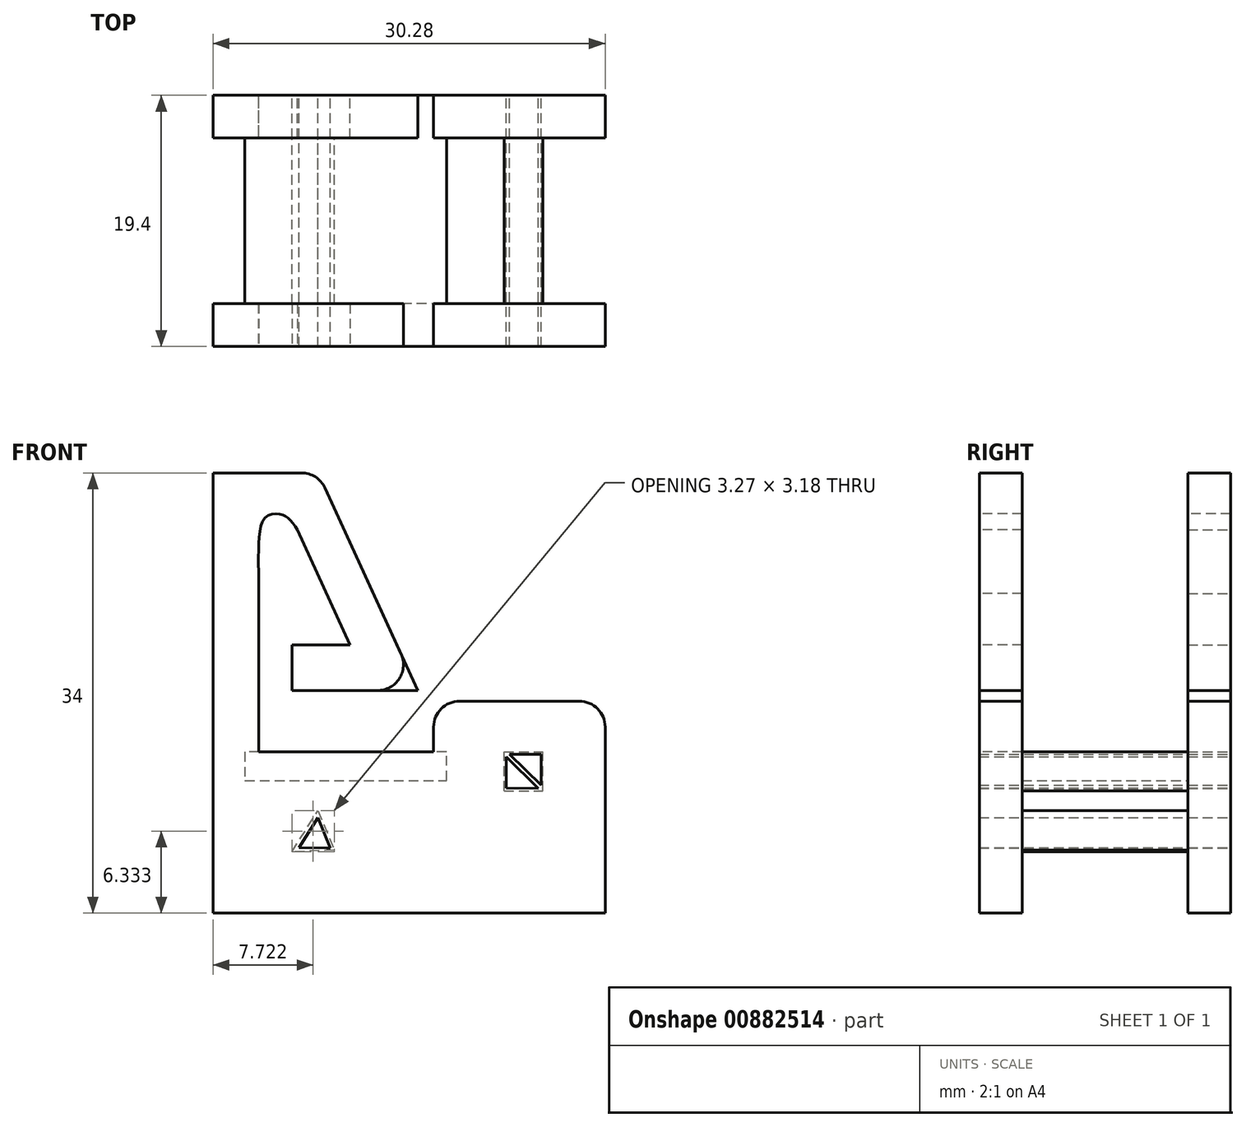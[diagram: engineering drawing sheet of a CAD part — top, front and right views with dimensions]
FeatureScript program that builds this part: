
annotation { "Feature Type Name" : "Feature", "Feature Type Description" : "" }
export const myFeature = defineFeature(function(context is Context, id is Id, definition is map)
    precondition{}
    {
        {
            var Q0;
            Q0=qCreatedBy(makeId("Front.planeOp"),FACE);
            var sketch = newSketch(context, id + "F0", { "sketchPlane" : qUnion([Q0])});
            skLineSegment(sketch, "E0", {"start": v(0, 0) * mm, "end": v(0, 34) * mm});
            skLineSegment(sketch, "E1", {"start": v(0, 34) * mm, "end": v(8.1, 34) * mm});
            skLineSegment(sketch, "E2", {"start": v(8.1, 34) * mm, "end": v(15.82, 17.2) * mm});
            skLineSegment(sketch, "E3", {"start": v(15.82, 17.2) * mm, "end": v(6.11, 17.2) * mm});
            skLineSegment(sketch, "E4", {"start": v(6.11, 17.2) * mm, "end": v(6.11, 20.72) * mm});
            skLineSegment(sketch, "E5", {"start": v(6.11, 20.72) * mm, "end": v(10.6, 20.72) * mm});
            skLineSegment(sketch, "E6", {"start": v(10.6, 20.72) * mm, "end": v(6.52, 29.6) * mm});
            skFitSpline(sketch, "E7", {"points": [v(6.52, 29.6) * mm, v(5.83, 30.48) * mm, v(5.16, 30.81) * mm, v(4.07, 30.57) * mm, v(3.54, 28.62) * mm, v(3.54, 24.67) * mm], "startDerivative": vector(-4.1, 6.02) * mm, "endDerivative": vector(0.29, -13.32) * mm});
            skLineSegment(sketch, "E8", {"start": v(3.54, 24.67) * mm, "end": v(3.54, 12.45) * mm});
            skLineSegment(sketch, "E9", {"start": v(3.54, 12.45) * mm, "end": v(2.46, 12.45) * mm});
            skLineSegment(sketch, "E10", {"start": v(2.46, 12.45) * mm, "end": v(2.46, 10.25) * mm});
            skLineSegment(sketch, "E11", {"start": v(2.46, 10.25) * mm, "end": v(18.04, 10.25) * mm});
            skLineSegment(sketch, "E12", {"start": v(18.04, 10.25) * mm, "end": v(18.04, 12.45) * mm});
            skLineSegment(sketch, "E13", {"start": v(18.04, 12.45) * mm, "end": v(17.04, 12.45) * mm});
            skLineSegment(sketch, "E14", {"start": v(17.04, 12.45) * mm, "end": v(17.04, 16.37) * mm});
            skLineSegment(sketch, "E15", {"start": v(17.04, 16.37) * mm, "end": v(30.28, 16.37) * mm});
            skLineSegment(sketch, "E16", {"start": v(30.28, 16.37) * mm, "end": v(30.28, 0) * mm});
            skLineSegment(sketch, "E17", {"start": v(30.28, 0) * mm, "end": v(0, 0) * mm});
            skLineSegment(sketch, "E18", {"start": v(22.47, 9.45) * mm, "end": v(22.47, 12.45) * mm});
            skLineSegment(sketch, "E19", {"start": v(22.47, 12.45) * mm, "end": v(25.47, 12.45) * mm});
            skLineSegment(sketch, "E20", {"start": v(22.47, 9.45) * mm, "end": v(25.47, 9.45) * mm});
            skLineSegment(sketch, "E21", {"start": v(25.47, 9.45) * mm, "end": v(25.47, 12.45) * mm});
            skSolve(sketch);
        }
        {
            var Q0;
            Q0 = qSketchRegion(id + "F0", true);
            extrude(context, id + "F1", {"entities" : qUnion([Q0]), "depth" : 3.3 * mm, "offsetDistance" : 25 * mm});
        }
        {
            var Q0;
            Q0=makeQuery(id+"F1.opExtrude","CAP_FACE",FACE,{"disambiguationData":[OSD([sQuery(id+"F0.wireOp",EDGE,"E0"),sQuery(id+"F0.wireOp",EDGE,"E1"),sQuery(id+"F0.wireOp",EDGE,"E2"),sQuery(id+"F0.wireOp",EDGE,"E3"),sQuery(id+"F0.wireOp",EDGE,"E4"),sQuery(id+"F0.wireOp",EDGE,"E5"),sQuery(id+"F0.wireOp",EDGE,"E6"),sQuery(id+"F0.wireOp",EDGE,"E7"),sQuery(id+"F0.wireOp",EDGE,"E8"),sQuery(id+"F0.wireOp",EDGE,"E9"),sQuery(id+"F0.wireOp",EDGE,"E10"),sQuery(id+"F0.wireOp",EDGE,"E11"),sQuery(id+"F0.wireOp",EDGE,"E12"),sQuery(id+"F0.wireOp",EDGE,"E13"),sQuery(id+"F0.wireOp",EDGE,"E14"),sQuery(id+"F0.wireOp",EDGE,"E15"),sQuery(id+"F0.wireOp",EDGE,"E16"),sQuery(id+"F0.wireOp",EDGE,"E17"),sQuery(id+"F0.wireOp",EDGE,"E18"),sQuery(id+"F0.wireOp",EDGE,"E19"),sQuery(id+"F0.wireOp",EDGE,"E20"),sQuery(id+"F0.wireOp",EDGE,"E21")])],"isStart":true});
            var sketch = newSketch(context, id + "F2", { "sketchPlane" : qUnion([Q0])});
            skLineSegment(sketch, "E22", {"start": v(-9.36, 4.88) * mm, "end": v(-8.1, 7.92) * mm});
            skLineSegment(sketch, "E23", {"start": v(-8.1, 7.92) * mm, "end": v(-6.09, 4.74) * mm});
            skLineSegment(sketch, "E24", {"start": v(-6.09, 4.74) * mm, "end": v(-9.36, 4.88) * mm});
            skLineSegment(sketch, "E25", {"start": v(-25.47, 9.45) * mm, "end": v(-22.47, 12.45) * mm});
            skLineSegment(sketch, "E26", {"start": v(-22.47, 12.45) * mm, "end": v(-25.47, 12.45) * mm});
            skLineSegment(sketch, "E27", {"start": v(-25.47, 12.45) * mm, "end": v(-25.47, 9.45) * mm});
            skLineSegment(sketch, "E28", {"start": v(-25.47, 9.45) * mm, "end": v(-22.47, 9.45) * mm});
            skLineSegment(sketch, "E29", {"start": v(-22.47, 9.45) * mm, "end": v(-22.47, 12.45) * mm});
            skLineSegment(sketch, "E30", {"start": v(-25.11, 9.63) * mm, "end": v(-22.65, 12.09) * mm});
            skLineSegment(sketch, "E31", {"start": v(-22.65, 12.09) * mm, "end": v(-22.65, 9.68) * mm});
            skLineSegment(sketch, "E32", {"start": v(-22.65, 9.68) * mm, "end": v(-25.11, 9.63) * mm});
            skLineSegment(sketch, "E33", {"start": v(-25.34, 9.89) * mm, "end": v(-25.34, 12.27) * mm});
            skLineSegment(sketch, "E34", {"start": v(-25.34, 12.27) * mm, "end": v(-22.9, 12.27) * mm});
            skLineSegment(sketch, "E35", {"start": v(-22.9, 12.27) * mm, "end": v(-25.34, 9.89) * mm});
            skLineSegment(sketch, "E36", {"start": v(-8.78, 5.03) * mm, "end": v(-9.04, 5.03) * mm});
            skLineSegment(sketch, "E37", {"start": v(-9.04, 5.03) * mm, "end": v(-8.1, 7.37) * mm});
            skLineSegment(sketch, "E38", {"start": v(-8.1, 7.37) * mm, "end": v(-6.62, 5.05) * mm});
            skLineSegment(sketch, "E39", {"start": v(-6.62, 5.05) * mm, "end": v(-8.78, 5.03) * mm});
            skSolve(sketch);
        }
        {
            var Q0;
            Q0 = qSketchRegion(id + "F2", true);
            extrude(context, id + "F3", {"entities" : qUnion([Q0]), "operationType" : NewBodyOperationType.ADD, "oppositeDirection" : true, "depth" : 9.7 * mm, "offsetDistance" : 25 * mm});
        }
        {
            var Q0;
            Q0=makeQuery(id+"F2.imprint","IMPRINT",FACE,{"disambiguationData":[TD([[makeQuery(id+"F2.imprint","IMPRINT",EDGE,{"derivedFrom":sQuery(id+"F2.wireOp",EDGE,"E36")}),-1.0]])]});
            extrude(context, id + "F4", {"entities" : qUnion([Q0]), "operationType" : NewBodyOperationType.REMOVE, "oppositeDirection" : true, "depth" : 25 * mm, "offsetDistance" : 25 * mm});
        }
        {
            var Q0;
            Q0=makeQuery(id+"F3.boolean.opBoolean","MERGE",FACE,{"derivedFrom":[makeQuery(id+"F1.opExtrude","CAP_FACE",FACE,{"disambiguationData":[OSD([sQuery(id+"F0.wireOp",EDGE,"E0"),sQuery(id+"F0.wireOp",EDGE,"E1"),sQuery(id+"F0.wireOp",EDGE,"E2"),sQuery(id+"F0.wireOp",EDGE,"E3"),sQuery(id+"F0.wireOp",EDGE,"E4"),sQuery(id+"F0.wireOp",EDGE,"E5"),sQuery(id+"F0.wireOp",EDGE,"E6"),sQuery(id+"F0.wireOp",EDGE,"E7"),sQuery(id+"F0.wireOp",EDGE,"E8"),sQuery(id+"F0.wireOp",EDGE,"E9"),sQuery(id+"F0.wireOp",EDGE,"E10"),sQuery(id+"F0.wireOp",EDGE,"E11"),sQuery(id+"F0.wireOp",EDGE,"E12"),sQuery(id+"F0.wireOp",EDGE,"E13"),sQuery(id+"F0.wireOp",EDGE,"E14"),sQuery(id+"F0.wireOp",EDGE,"E15"),sQuery(id+"F0.wireOp",EDGE,"E16"),sQuery(id+"F0.wireOp",EDGE,"E17"),sQuery(id+"F0.wireOp",EDGE,"E18"),sQuery(id+"F0.wireOp",EDGE,"E19"),sQuery(id+"F0.wireOp",EDGE,"E20"),sQuery(id+"F0.wireOp",EDGE,"E21")])],"isStart":true}),makeQuery(id+"F3.opExtrude","CAP_FACE",FACE,{"disambiguationData":[OSD([sQuery(id+"F2.wireOp",EDGE,"E26"),sQuery(id+"F2.wireOp",EDGE,"E27"),sQuery(id+"F2.wireOp",EDGE,"E28"),sQuery(id+"F2.wireOp",EDGE,"E29"),sQuery(id+"F2.wireOp",EDGE,"E30"),sQuery(id+"F2.wireOp",EDGE,"E31"),sQuery(id+"F2.wireOp",EDGE,"E32"),sQuery(id+"F2.wireOp",EDGE,"E33"),sQuery(id+"F2.wireOp",EDGE,"E34"),sQuery(id+"F2.wireOp",EDGE,"E35")])],"isStart":true})]});
            var sketch = newSketch(context, id + "F5", { "sketchPlane" : qUnion([Q0])});
            skLineSegment(sketch, "E40", {"start": v(-18.04, 10.25) * mm, "end": v(-18.04, 12.45) * mm});
            skLineSegment(sketch, "E41", {"start": v(-18.04, 12.45) * mm, "end": v(-2.46, 12.45) * mm});
            skLineSegment(sketch, "E42", {"start": v(-2.46, 12.45) * mm, "end": v(-2.46, 10.25) * mm});
            skLineSegment(sketch, "E43", {"start": v(-2.46, 10.25) * mm, "end": v(-18.04, 10.25) * mm});
            skSolve(sketch);
        }
        {
            var Q0;
            Q0 = qSketchRegion(id + "F5", true);
            extrude(context, id + "F6", {"entities" : qUnion([Q0]), "operationType" : NewBodyOperationType.ADD, "oppositeDirection" : true, "depth" : 9.7 * mm, "offsetDistance" : 25 * mm});
        }
        {
            var Q0;
            Q0=makeQuery(id+"F1.opExtrude","SWEPT_BODY",BODY,{"disambiguationData":[OSD([sQuery(id+"F0.wireOp",EDGE,"E0"),sQuery(id+"F0.wireOp",EDGE,"E1"),sQuery(id+"F0.wireOp",EDGE,"E2"),sQuery(id+"F0.wireOp",EDGE,"E3"),sQuery(id+"F0.wireOp",EDGE,"E4"),sQuery(id+"F0.wireOp",EDGE,"E5"),sQuery(id+"F0.wireOp",EDGE,"E6"),sQuery(id+"F0.wireOp",EDGE,"E7"),sQuery(id+"F0.wireOp",EDGE,"E8"),sQuery(id+"F0.wireOp",EDGE,"E9"),sQuery(id+"F0.wireOp",EDGE,"E10"),sQuery(id+"F0.wireOp",EDGE,"E11"),sQuery(id+"F0.wireOp",EDGE,"E12"),sQuery(id+"F0.wireOp",EDGE,"E13"),sQuery(id+"F0.wireOp",EDGE,"E14"),sQuery(id+"F0.wireOp",EDGE,"E15"),sQuery(id+"F0.wireOp",EDGE,"E16"),sQuery(id+"F0.wireOp",EDGE,"E17"),sQuery(id+"F0.wireOp",EDGE,"E18"),sQuery(id+"F0.wireOp",EDGE,"E19"),sQuery(id+"F0.wireOp",EDGE,"E20"),sQuery(id+"F0.wireOp",EDGE,"E21")])]});
            var Q1;
            Q1=makeQuery(id+"F6.opExtrude","CAP_FACE",FACE,{"disambiguationData":[OSD([sQuery(id+"F5.wireOp",EDGE,"E40"),sQuery(id+"F5.wireOp",EDGE,"E41"),sQuery(id+"F5.wireOp",EDGE,"E42"),sQuery(id+"F5.wireOp",EDGE,"E43")])],"isStart":false});
            mirror(context, id + "F7", {"operationType" : NewBodyOperationType.ADD, "entities" : qUnion([Q0]), "mirrorPlane" : qUnion([Q1])});
        }
        {
            var Q0;
            Q0=makeQuery(id+"F7.opPattern","COPY",EDGE,{"derivedFrom":makeQuery(id+"F1.opExtrude","SWEPT_EDGE",EDGE,{"disambiguationData":[OSD([sQuery(id+"F0.wireOp",EDGE,"E15"),sQuery(id+"F0.wireOp",EDGE,"E16")])]}),"instanceName":"1"});
            var Q1;
            Q1=makeQuery(id+"F1.opExtrude","SWEPT_EDGE",EDGE,{"disambiguationData":[OSD([sQuery(id+"F0.wireOp",EDGE,"E15"),sQuery(id+"F0.wireOp",EDGE,"E16")])]});
            var Q2;
            Q2=makeQuery(id+"F7.opPattern","COPY",EDGE,{"derivedFrom":makeQuery(id+"F1.opExtrude","SWEPT_EDGE",EDGE,{"disambiguationData":[OSD([sQuery(id+"F0.wireOp",EDGE,"E1"),sQuery(id+"F0.wireOp",EDGE,"E2")])]}),"instanceName":"1"});
            var Q3;
            Q3=makeQuery(id+"F1.opExtrude","SWEPT_EDGE",EDGE,{"disambiguationData":[OSD([sQuery(id+"F0.wireOp",EDGE,"E1"),sQuery(id+"F0.wireOp",EDGE,"E2")])]});
            var Q4;
            Q4=makeQuery(id+"F7.opPattern","COPY",EDGE,{"derivedFrom":makeQuery(id+"F1.opExtrude","SWEPT_EDGE",EDGE,{"disambiguationData":[OSD([sQuery(id+"F0.wireOp",EDGE,"E2"),sQuery(id+"F0.wireOp",EDGE,"E3")])]}),"instanceName":"1"});
            var Q5;
            Q5=makeQuery(id+"F7.opPattern","COPY",EDGE,{"derivedFrom":makeQuery(id+"F1.opExtrude","SWEPT_EDGE",EDGE,{"disambiguationData":[OSD([sQuery(id+"F0.wireOp",EDGE,"E14"),sQuery(id+"F0.wireOp",EDGE,"E15")])]}),"instanceName":"1"});
            var Q6;
            Q6=makeQuery(id+"F1.opExtrude","SWEPT_EDGE",EDGE,{"disambiguationData":[OSD([sQuery(id+"F0.wireOp",EDGE,"E14"),sQuery(id+"F0.wireOp",EDGE,"E15")])]});
            fillet(context, id + "F8", {"entities" : qUnion([Q0, Q1, Q2, Q3, Q4, Q5, Q6]), "radius" : 2 * mm, "tangentPropagation" : true, "allowEdgeOverflow" : false});
        }
    });
